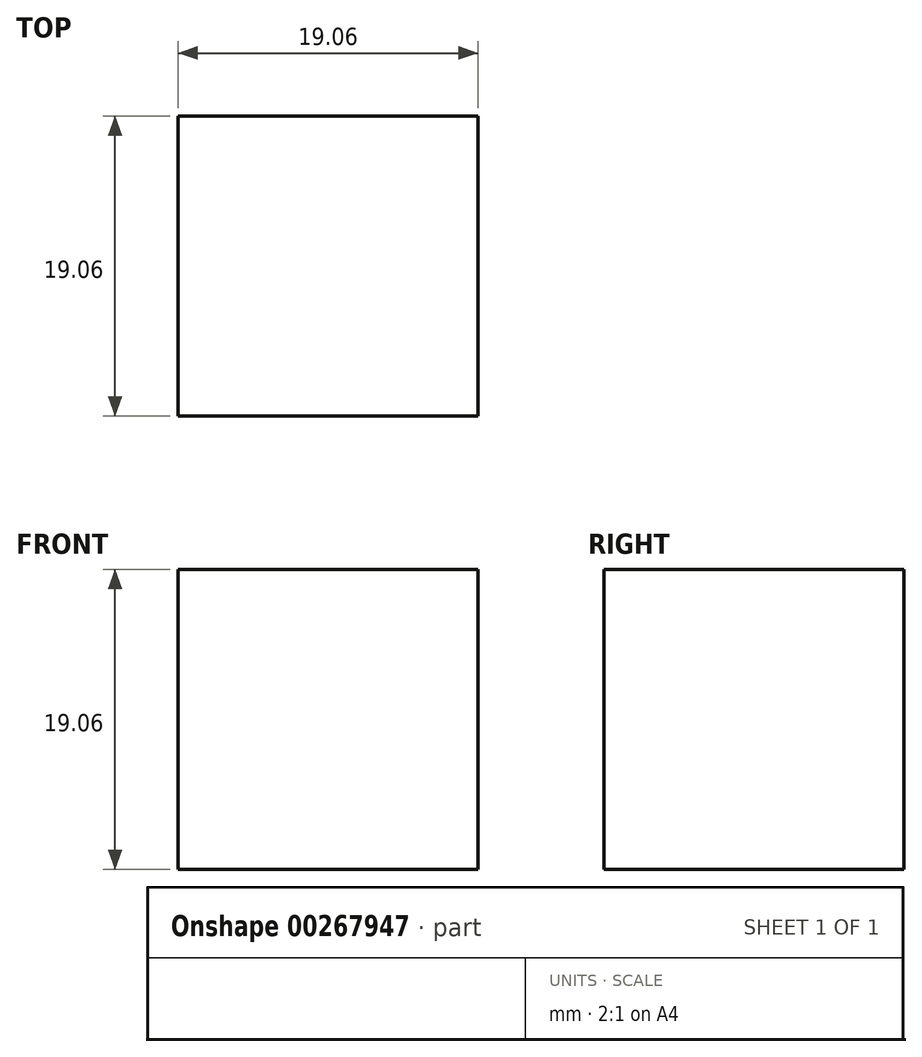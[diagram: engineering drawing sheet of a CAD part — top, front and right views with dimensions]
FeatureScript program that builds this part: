
annotation { "Feature Type Name" : "Feature", "Feature Type Description" : "" }
export const myFeature = defineFeature(function(context is Context, id is Id, definition is map)
    precondition{}
    {
        {
            var Q0;
            Q0=qCreatedBy(makeId("Front.planeOp"),FACE);
            var sketch = newSketch(context, id + "F0", { "sketchPlane" : qUnion([Q0])});
            skLineSegment(sketch, "E0.bottom", {"start": v(9.53, 9.52) * mm, "end": v(-9.52, 9.52) * mm});
            skLineSegment(sketch, "E0.top", {"start": v(9.53, -9.53) * mm, "end": v(-9.52, -9.53) * mm});
            skLineSegment(sketch, "E0.left", {"start": v(9.53, 9.52) * mm, "end": v(9.53, -9.53) * mm});
            skLineSegment(sketch, "E0.right", {"start": v(-9.53, 9.52) * mm, "end": v(-9.53, -9.53) * mm});
            skPoint(sketch, "E0.middle", {"position": v(0, 0) * mm});
            skSolve(sketch);
        }
        {
            var Q0;
            Q0 = qSketchRegion(id + "F0", true);
            extrude(context, id + "F1", {"entities" : qUnion([Q0]), "endBound" : BoundingType.SYMMETRIC, "depth" : 19.05 * mm});
        }
    });
